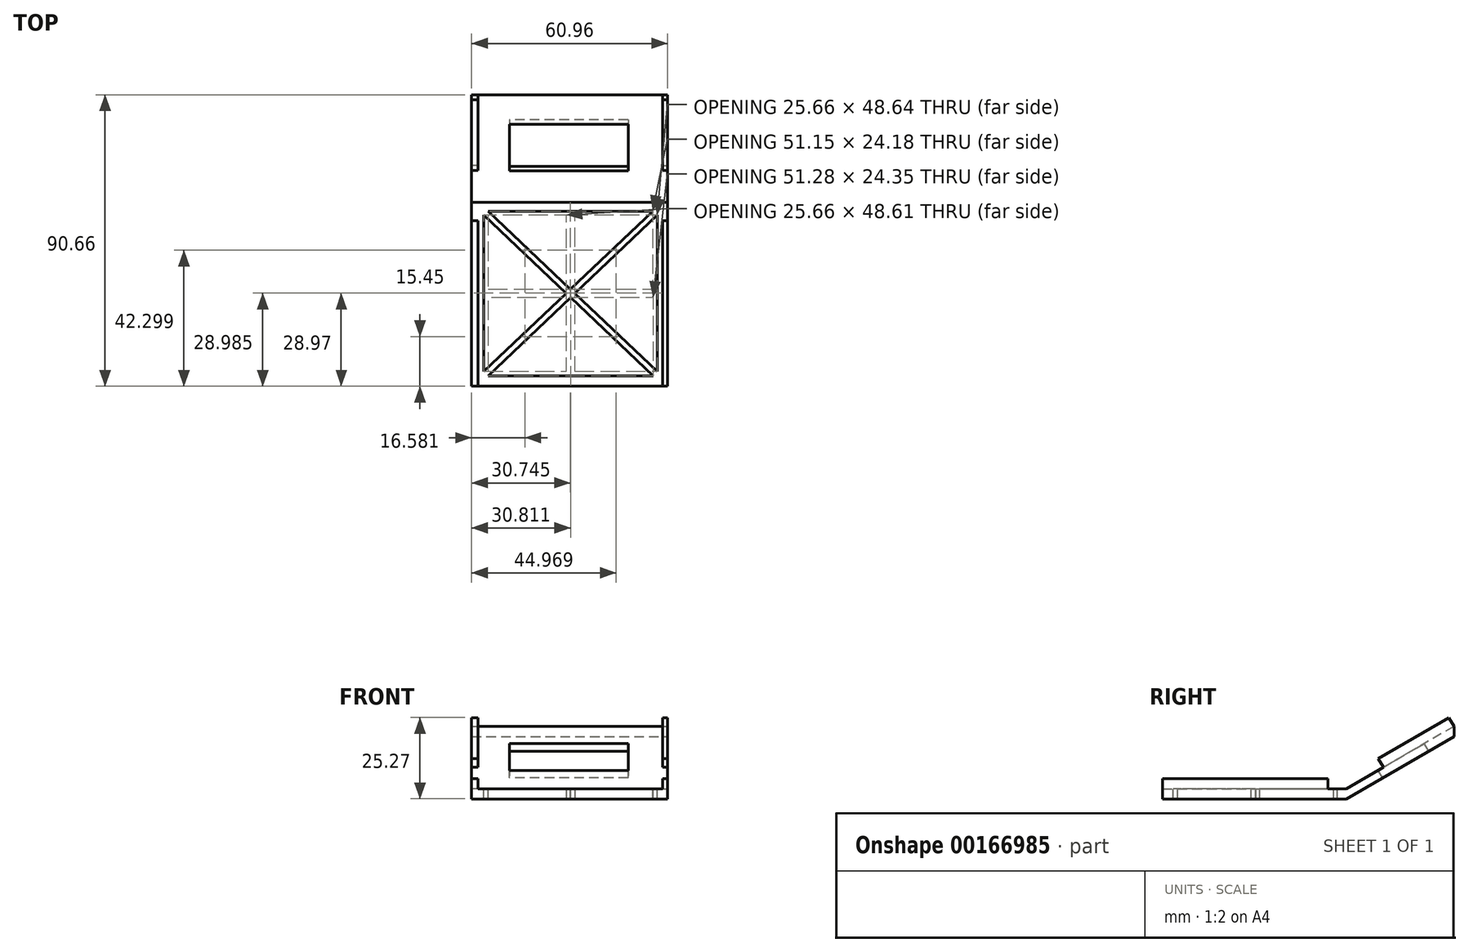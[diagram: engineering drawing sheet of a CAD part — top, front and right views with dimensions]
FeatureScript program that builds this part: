
annotation { "Feature Type Name" : "Feature", "Feature Type Description" : "" }
export const myFeature = defineFeature(function(context is Context, id is Id, definition is map)
    precondition{}
    {
        {
            var Q0;
            Q0=qCreatedBy(makeId("Right.planeOp"),FACE);
            var sketch = newSketch(context, id + "F0", { "sketchPlane" : qUnion([Q0])});
            skLineSegment(sketch, "E0.bottom", {"start": v(24.73, -0.82) * mm, "end": v(-32.42, -0.82) * mm});
            skLineSegment(sketch, "E0.top", {"start": v(24.73, 2.35) * mm, "end": v(-32.42, 2.35) * mm});
            skLineSegment(sketch, "E0.right", {"start": v(-32.42, -0.82) * mm, "end": v(-32.42, 2.35) * mm});
            skPoint(sketch, "E0.middle", {"position": v(-3.85, 0.76) * mm});
            skLineSegment(sketch, "E1", {"start": v(24.73, 2.35) * mm, "end": v(68.72, 27.75) * mm});
            skLineSegment(sketch, "E2", {"start": v(68.72, 27.75) * mm, "end": v(68.72, 24.58) * mm});
            skLineSegment(sketch, "E3", {"start": v(68.72, 24.58) * mm, "end": v(24.73, -0.82) * mm});
            skSolve(sketch);
        }
        {
            var Q0;
            Q0 = qSketchRegion(id + "F0", true);
            extrude(context, id + "F1", {"entities" : qUnion([Q0]), "depth" : 60.96 * mm});
        }
        {
            var Q0;
            Q0=makeQuery(id+"F1.opExtrude","SWEPT_FACE",FACE,{"disambiguationData":[OSD([sQuery(id+"F0.wireOp",EDGE,"E0.top")])]});
            var sketch = newSketch(context, id + "F2", { "sketchPlane" : qUnion([Q0])});
            skLineSegment(sketch, "E4", {"start": v(60.96, -32.42) * mm, "end": v(59.37, -32.42) * mm});
            skLineSegment(sketch, "E5", {"start": v(59.37, -32.42) * mm, "end": v(59.37, 0) * mm});
            skLineSegment(sketch, "E6", {"start": v(59.37, 0) * mm, "end": v(60.96, 0) * mm});
            skLineSegment(sketch, "E7", {"start": v(60.96, 0) * mm, "end": v(60.96, -32.42) * mm});
            skSolve(sketch);
        }
        {
            var Q0;
            Q0 = qSketchRegion(id + "F2", true);
            extrude(context, id + "F3", {"entities" : qUnion([Q0]), "operationType" : NewBodyOperationType.ADD, "depth" : 3.17 * mm});
        }
        {
            var Q0;
            Q0=makeQuery(id+"F1.opExtrude","SWEPT_FACE",FACE,{"disambiguationData":[OSD([sQuery(id+"F0.wireOp",EDGE,"E0.top")])]});
            var sketch = newSketch(context, id + "F4", { "sketchPlane" : qUnion([Q0])});
            skLineSegment(sketch, "E8", {"start": v(0, -32.42) * mm, "end": v(1.59, -32.42) * mm});
            skLineSegment(sketch, "E9", {"start": v(1.59, -32.42) * mm, "end": v(1.59, 0) * mm});
            skLineSegment(sketch, "E10", {"start": v(1.59, 0) * mm, "end": v(0, 0) * mm});
            skLineSegment(sketch, "E11", {"start": v(0, 0) * mm, "end": v(0, -32.42) * mm});
            skSolve(sketch);
        }
        {
            var Q0;
            Q0 = qSketchRegion(id + "F4", true);
            extrude(context, id + "F5", {"entities" : qUnion([Q0]), "operationType" : NewBodyOperationType.ADD, "depth" : 3.17 * mm});
        }
        {
            var Q0;
            Q0=makeQuery(id+"F3.boolean.opBoolean","MERGE",FACE,{"derivedFrom":[makeQuery(id+"F1.opExtrude","CAP_FACE",FACE,{"disambiguationData":[OSD([sQuery(id+"F0.wireOp",EDGE,"E0.bottom"),sQuery(id+"F0.wireOp",EDGE,"E0.top"),sQuery(id+"F0.wireOp",EDGE,"E0.right"),sQuery(id+"F0.wireOp",EDGE,"E1"),sQuery(id+"F0.wireOp",EDGE,"E2"),sQuery(id+"F0.wireOp",EDGE,"E3")])],"isStart":false}),makeQuery(id+"F3.opExtrude","SWEPT_FACE",FACE,{"disambiguationData":[OSD([sQuery(id+"F2.wireOp",EDGE,"E7")])]})]});
            var sketch = newSketch(context, id + "F6", { "sketchPlane" : qUnion([Q0])});
            skLineSegment(sketch, "E12", {"start": v(58.24, 21.7) * mm, "end": v(58.24, 18.52) * mm});
            skLineSegment(sketch, "E13", {"start": v(58.24, 18.52) * mm, "end": v(68.72, 24.58) * mm});
            skLineSegment(sketch, "E14", {"start": v(68.72, 24.58) * mm, "end": v(68.72, 27.75) * mm});
            skLineSegment(sketch, "E15", {"start": v(68.72, 27.75) * mm, "end": v(58.24, 21.7) * mm});
            skSolve(sketch);
        }
        {
            var Q0;
            Q0=makeQuery(id+"F6.imprint","IMPRINT",FACE,{"disambiguationData":[TD([[makeQuery(id+"F6.imprint","IMPRINT",EDGE,{"derivedFrom":sQuery(id+"F6.wireOp",EDGE,"E12")}),1.0]])]});
            extrude(context, id + "F7", {"entities" : qUnion([Q0]), "operationType" : NewBodyOperationType.REMOVE, "endBound" : BoundingType.THROUGH_ALL, "oppositeDirection" : true, "depth" : 25.4 * mm});
        }
        {
            var Q0;
            Q0=makeQuery(id+"F1.opExtrude","SWEPT_FACE",FACE,{"disambiguationData":[OSD([sQuery(id+"F0.wireOp",EDGE,"E0.top")])]});
            var sketch = newSketch(context, id + "F8", { "sketchPlane" : qUnion([Q0])});
            skLineSegment(sketch, "E16.bottom", {"start": v(3.75, -29.15) * mm, "end": v(57.8, -29.15) * mm});
            skLineSegment(sketch, "E16.top", {"start": v(3.75, 21.97) * mm, "end": v(57.8, 21.97) * mm});
            skLineSegment(sketch, "E16.left", {"start": v(3.75, -29.15) * mm, "end": v(3.75, 21.97) * mm});
            skLineSegment(sketch, "E16.right", {"start": v(57.8, -29.15) * mm, "end": v(57.8, 21.97) * mm});
            skSolve(sketch);
        }
        {
            var Q0;
            Q0 = qSketchRegion(id + "F8", true);
            extrude(context, id + "F9", {"entities" : qUnion([Q0]), "operationType" : NewBodyOperationType.REMOVE, "endBound" : BoundingType.THROUGH_ALL, "oppositeDirection" : true, "depth" : 25.4 * mm});
        }
        {
            var Q0;
            Q0=makeQuery(id+"F1.opExtrude","SWEPT_FACE",FACE,{"disambiguationData":[OSD([sQuery(id+"F0.wireOp",EDGE,"E1")])]});
            var sketch = newSketch(context, id + "F10", { "sketchPlane" : qUnion([Q0])});
            skLineSegment(sketch, "E17", {"start": v(60.96, 61.29) * mm, "end": v(59.37, 61.29) * mm});
            skLineSegment(sketch, "E18", {"start": v(59.37, 61.29) * mm, "end": v(59.37, 35.89) * mm});
            skLineSegment(sketch, "E19", {"start": v(59.37, 35.89) * mm, "end": v(60.96, 35.89) * mm});
            skLineSegment(sketch, "E20", {"start": v(60.96, 35.89) * mm, "end": v(60.96, 61.29) * mm});
            skSolve(sketch);
        }
        {
            var Q0;
            Q0 = qSketchRegion(id + "F10", true);
            extrude(context, id + "F11", {"entities" : qUnion([Q0]), "operationType" : NewBodyOperationType.ADD, "depth" : 3.17 * mm});
        }
        {
            var Q0;
            Q0=makeQuery(id+"F1.opExtrude","SWEPT_FACE",FACE,{"disambiguationData":[OSD([sQuery(id+"F0.wireOp",EDGE,"E1")])]});
            var sketch = newSketch(context, id + "F12", { "sketchPlane" : qUnion([Q0])});
            skLineSegment(sketch, "E21", {"start": v(0, 61.29) * mm, "end": v(1.59, 61.29) * mm});
            skLineSegment(sketch, "E22", {"start": v(1.59, 61.29) * mm, "end": v(1.59, 35.89) * mm});
            skLineSegment(sketch, "E23", {"start": v(1.59, 35.89) * mm, "end": v(0, 35.89) * mm});
            skLineSegment(sketch, "E24", {"start": v(0, 35.89) * mm, "end": v(0, 61.29) * mm});
            skSolve(sketch);
        }
        {
            var Q0;
            Q0 = qSketchRegion(id + "F12", true);
            extrude(context, id + "F13", {"entities" : qUnion([Q0]), "operationType" : NewBodyOperationType.ADD, "depth" : 3.17 * mm});
        }
        {
            var Q0;
            Q0=makeQuery(id+"F1.opExtrude","SWEPT_FACE",FACE,{"disambiguationData":[OSD([sQuery(id+"F0.wireOp",EDGE,"E0.top")])]});
            var sketch = newSketch(context, id + "F14", { "sketchPlane" : qUnion([Q0])});
            skLineSegment(sketch, "E25", {"start": v(5.17, 21.97) * mm, "end": v(57.8, -27.77) * mm});
            skLineSegment(sketch, "E26", {"start": v(57.8, -27.77) * mm, "end": v(57.8, -29.15) * mm});
            skLineSegment(sketch, "E27", {"start": v(57.8, -29.15) * mm, "end": v(56.45, -29.15) * mm});
            skLineSegment(sketch, "E28", {"start": v(56.45, -29.15) * mm, "end": v(3.75, 20.87) * mm});
            skLineSegment(sketch, "E29", {"start": v(3.75, 20.87) * mm, "end": v(3.75, 21.97) * mm});
            skLineSegment(sketch, "E30", {"start": v(3.75, 21.97) * mm, "end": v(5.17, 21.97) * mm});
            skSolve(sketch);
        }
        {
            var Q0;
            Q0 = qSketchRegion(id + "F14", true);
            extrude(context, id + "F15", {"entities" : qUnion([Q0]), "operationType" : NewBodyOperationType.ADD, "oppositeDirection" : true, "depth" : 3.17 * mm});
        }
        {
            var Q0;
            Q0=makeQuery(id+"F15.boolean.opBoolean","MERGE",FACE,{"derivedFrom":[makeQuery(id+"F1.opExtrude","SWEPT_FACE",FACE,{"disambiguationData":[OSD([sQuery(id+"F0.wireOp",EDGE,"E0.top")])]}),makeQuery(id+"F15.opExtrude","CAP_FACE",FACE,{"disambiguationData":[OSD([sQuery(id+"F14.wireOp",EDGE,"E25"),sQuery(id+"F14.wireOp",EDGE,"E26"),sQuery(id+"F14.wireOp",EDGE,"E27"),sQuery(id+"F14.wireOp",EDGE,"E28"),sQuery(id+"F14.wireOp",EDGE,"E29"),sQuery(id+"F14.wireOp",EDGE,"E30")])],"isStart":true})]});
            var sketch = newSketch(context, id + "F16", { "sketchPlane" : qUnion([Q0])});
            skLineSegment(sketch, "E31", {"start": v(3.75, -27.74) * mm, "end": v(56.32, 21.97) * mm});
            skLineSegment(sketch, "E32", {"start": v(56.32, 21.97) * mm, "end": v(57.8, 21.97) * mm});
            skLineSegment(sketch, "E33", {"start": v(57.8, 21.97) * mm, "end": v(57.8, 20.87) * mm});
            skLineSegment(sketch, "E34", {"start": v(57.8, 20.87) * mm, "end": v(5.17, -29.15) * mm});
            skLineSegment(sketch, "E35", {"start": v(5.17, -29.15) * mm, "end": v(3.75, -29.15) * mm});
            skLineSegment(sketch, "E36", {"start": v(3.75, -29.15) * mm, "end": v(3.75, -27.74) * mm});
            skSolve(sketch);
        }
        {
            var Q0;
            Q0 = qSketchRegion(id + "F16", true);
            extrude(context, id + "F17", {"entities" : qUnion([Q0]), "operationType" : NewBodyOperationType.ADD, "oppositeDirection" : true, "depth" : 3.17 * mm});
        }
        {
            var Q0;
            Q0=makeQuery(id+"F1.opExtrude","SWEPT_FACE",FACE,{"disambiguationData":[OSD([sQuery(id+"F0.wireOp",EDGE,"E1")])]});
            var sketch = newSketch(context, id + "F18", { "sketchPlane" : qUnion([Q0])});
            skLineSegment(sketch, "E37.bottom", {"start": v(11.73, 34) * mm, "end": v(48.72, 34) * mm});
            skLineSegment(sketch, "E37.top", {"start": v(11.73, 50.66) * mm, "end": v(48.72, 50.66) * mm});
            skLineSegment(sketch, "E37.left", {"start": v(11.73, 34) * mm, "end": v(11.73, 50.66) * mm});
            skLineSegment(sketch, "E37.right", {"start": v(48.72, 34) * mm, "end": v(48.72, 50.66) * mm});
            skSolve(sketch);
        }
        {
            var Q0;
            Q0 = qSketchRegion(id + "F18", true);
            extrude(context, id + "F19", {"entities" : qUnion([Q0]), "operationType" : NewBodyOperationType.REMOVE, "endBound" : BoundingType.THROUGH_ALL, "oppositeDirection" : true, "depth" : 25.4 * mm});
        }
        {
            var Q0;
            Q0=makeQuery(id+"F13.opExtrude","SWEPT_FACE",FACE,{"disambiguationData":[OSD([sQuery(id+"F12.wireOp",EDGE,"E22")])]});
            extrude(context, id + "F20", {"entities" : qUnion([Q0]), "operationType" : NewBodyOperationType.ADD, "depth" : 0.4 * mm});
        }
        {
            var Q0;
            Q0=makeQuery(id+"F5.opExtrude","SWEPT_FACE",FACE,{"disambiguationData":[OSD([sQuery(id+"F4.wireOp",EDGE,"E9")])]});
            extrude(context, id + "F21", {"entities" : qUnion([Q0]), "operationType" : NewBodyOperationType.ADD, "depth" : 0.4 * mm});
        }
        {
            var Q0;
            {var subQ0=sQuery(id+"F4.wireOp",EDGE,"E10");Q0=makeQuery(id+"F21.boolean.opBoolean","MERGE",FACE,{"derivedFrom":[makeQuery(id+"F5.opExtrude","SWEPT_FACE",FACE,{"disambiguationData":[OSD([subQ0])]}),makeQuery(id+"F21.opExtrude","SWEPT_FACE",FACE,{"disambiguationData":[OSD([sQuery(id+"F4.wireOp",EDGE,"E9"),subQ0])]})]});}
            extrude(context, id + "F22", {"entities" : qUnion([Q0]), "operationType" : NewBodyOperationType.ADD, "depth" : 19.05 * mm});
        }
        {
            var Q0;
            Q0=makeQuery(id+"F3.opExtrude","SWEPT_FACE",FACE,{"disambiguationData":[OSD([sQuery(id+"F2.wireOp",EDGE,"E6")])]});
            extrude(context, id + "F23", {"entities" : qUnion([Q0]), "operationType" : NewBodyOperationType.ADD, "depth" : 19.05 * mm});
        }
    });
